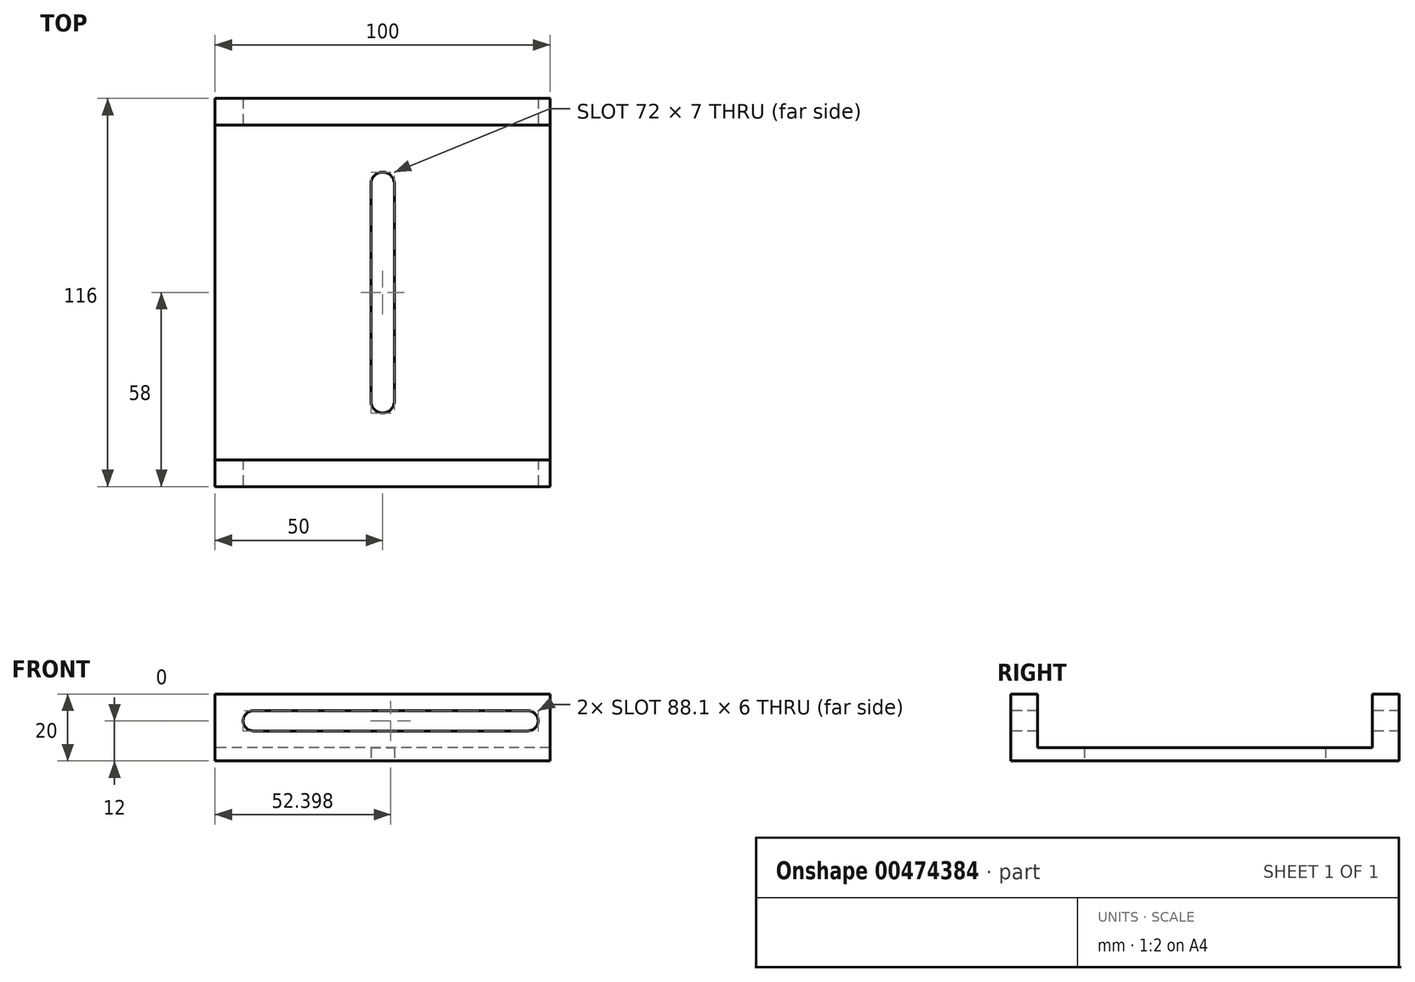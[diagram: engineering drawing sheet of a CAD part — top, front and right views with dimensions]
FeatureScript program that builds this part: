
annotation { "Feature Type Name" : "Feature", "Feature Type Description" : "" }
export const myFeature = defineFeature(function(context is Context, id is Id, definition is map)
    precondition{}
    {
        {
            var Q0;
            Q0=qCreatedBy(makeId("Top.planeOp"),FACE);
            var sketch = newSketch(context, id + "F0", { "sketchPlane" : qUnion([Q0])});
            skLineSegment(sketch, "E0.bottom", {"start": v(50, 50) * mm, "end": v(-50, 50) * mm});
            skLineSegment(sketch, "E0.top", {"start": v(50, -50) * mm, "end": v(-50, -50) * mm});
            skLineSegment(sketch, "E0.left", {"start": v(50, 50) * mm, "end": v(50, -50) * mm});
            skLineSegment(sketch, "E0.right", {"start": v(-50, 50) * mm, "end": v(-50, -50) * mm});
            skPoint(sketch, "E0.middle", {"position": v(0, 0) * mm});
            skLineSegment(sketch, "E1.left", {"start": v(3.5, -32.5) * mm, "end": v(3.5, 32.5) * mm});
            skLineSegment(sketch, "E1.right", {"start": v(-3.5, -32.5) * mm, "end": v(-3.5, 32.5) * mm});
            skArc(sketch, "E2", {"start": v(-3.5, -32.5) * mm, "mid": v(0, -36) * mm, "end": v(3.5, -32.5) * mm});
            skArc(sketch, "E3", {"start": v(3.5, 32.5) * mm, "mid": v(0, 36) * mm, "end": v(-3.5, 32.5) * mm});
            skSolve(sketch);
        }
        {
            var Q0;
            Q0 = qSketchRegion(id + "F0", true);
            extrude(context, id + "F1", {"entities" : qUnion([Q0]), "depth" : 4 * mm});
        }
        {
            var Q0;
            Q0=qCreatedBy(makeId("Top.planeOp"),FACE);
            var sketch = newSketch(context, id + "F2", { "sketchPlane" : qUnion([Q0])});
            skLineSegment(sketch, "E4.0", {"start": v(50, 50) * mm, "end": v(-50, 50) * mm});
            skLineSegment(sketch, "E5.0", {"start": v(50, -50) * mm, "end": v(-50, -50) * mm});
            skLineSegment(sketch, "E6.bottom", {"start": v(-50, 50) * mm, "end": v(50, 50) * mm});
            skLineSegment(sketch, "E6.top", {"start": v(-50, 58) * mm, "end": v(50, 58) * mm});
            skLineSegment(sketch, "E6.left", {"start": v(-50, 50) * mm, "end": v(-50, 58) * mm});
            skLineSegment(sketch, "E6.right", {"start": v(50, 50) * mm, "end": v(50, 58) * mm});
            skLineSegment(sketch, "E7.bottom", {"start": v(-50, -50) * mm, "end": v(50, -50) * mm});
            skLineSegment(sketch, "E7.top", {"start": v(-50, -58) * mm, "end": v(50, -58) * mm});
            skLineSegment(sketch, "E7.left", {"start": v(-50, -50) * mm, "end": v(-50, -58) * mm});
            skLineSegment(sketch, "E7.right", {"start": v(50, -50) * mm, "end": v(50, -58) * mm});
            skSolve(sketch);
        }
        {
            var Q0;
            Q0 = qSketchRegion(id + "F2", true);
            extrude(context, id + "F3", {"entities" : qUnion([Q0]), "operationType" : NewBodyOperationType.ADD, "depth" : 20 * mm});
        }
        {
            var Q0;
            Q0=qCreatedBy(makeId("Front.planeOp"),FACE);
            var sketch = newSketch(context, id + "F4", { "sketchPlane" : qUnion([Q0])});
            skLineSegment(sketch, "E8.0.0", {"start": v(-50, 4) * mm, "end": v(50, 4) * mm});
            skLineSegment(sketch, "E8.0.1", {"start": v(50, 4) * mm, "end": v(50, 20) * mm, "construction": true});
            skLineSegment(sketch, "E8.0.2", {"start": v(50, 20) * mm, "end": v(-50, 20) * mm, "construction": true});
            skLineSegment(sketch, "E8.0.3", {"start": v(-50, 20) * mm, "end": v(-50, 4) * mm, "construction": true});
            skLineSegment(sketch, "E9.0.2", {"start": v(50, 4) * mm, "end": v(-50, 4) * mm, "construction": true});
            skLineSegment(sketch, "E10.bottom", {"start": v(-38.65, 9) * mm, "end": v(43.45, 9) * mm});
            skLineSegment(sketch, "E10.top", {"start": v(-38.65, 15) * mm, "end": v(43.45, 15) * mm});
            skLineSegment(sketch, "E10.left", {"start": v(-38.65, 9) * mm, "end": v(-38.65, 15) * mm, "construction": true});
            skLineSegment(sketch, "E10.right", {"start": v(43.45, 9) * mm, "end": v(43.45, 15) * mm, "construction": true});
            skArc(sketch, "E11", {"start": v(43.45, 15) * mm, "mid": v(46.45, 12) * mm, "end": v(43.45, 9) * mm});
            skArc(sketch, "E12", {"start": v(-38.65, 15) * mm, "mid": v(-41.65, 12) * mm, "end": v(-38.65, 9) * mm});
            skSolve(sketch);
        }
        {
            var Q0;
            Q0 = qSketchRegion(id + "F4", true);
            extrude(context, id + "F5", {"entities" : qUnion([Q0]), "operationType" : NewBodyOperationType.REMOVE, "endBound" : BoundingType.THROUGH_ALL, "oppositeDirection" : true, "depth" : 25 * mm, "hasSecondDirection" : true, "secondDirectionBound" : SecondDirectionBoundingType.THROUGH_ALL, "secondDirectionOppositeDirection" : false, "secondDirectionDepth" : 25 * mm});
        }
    });
